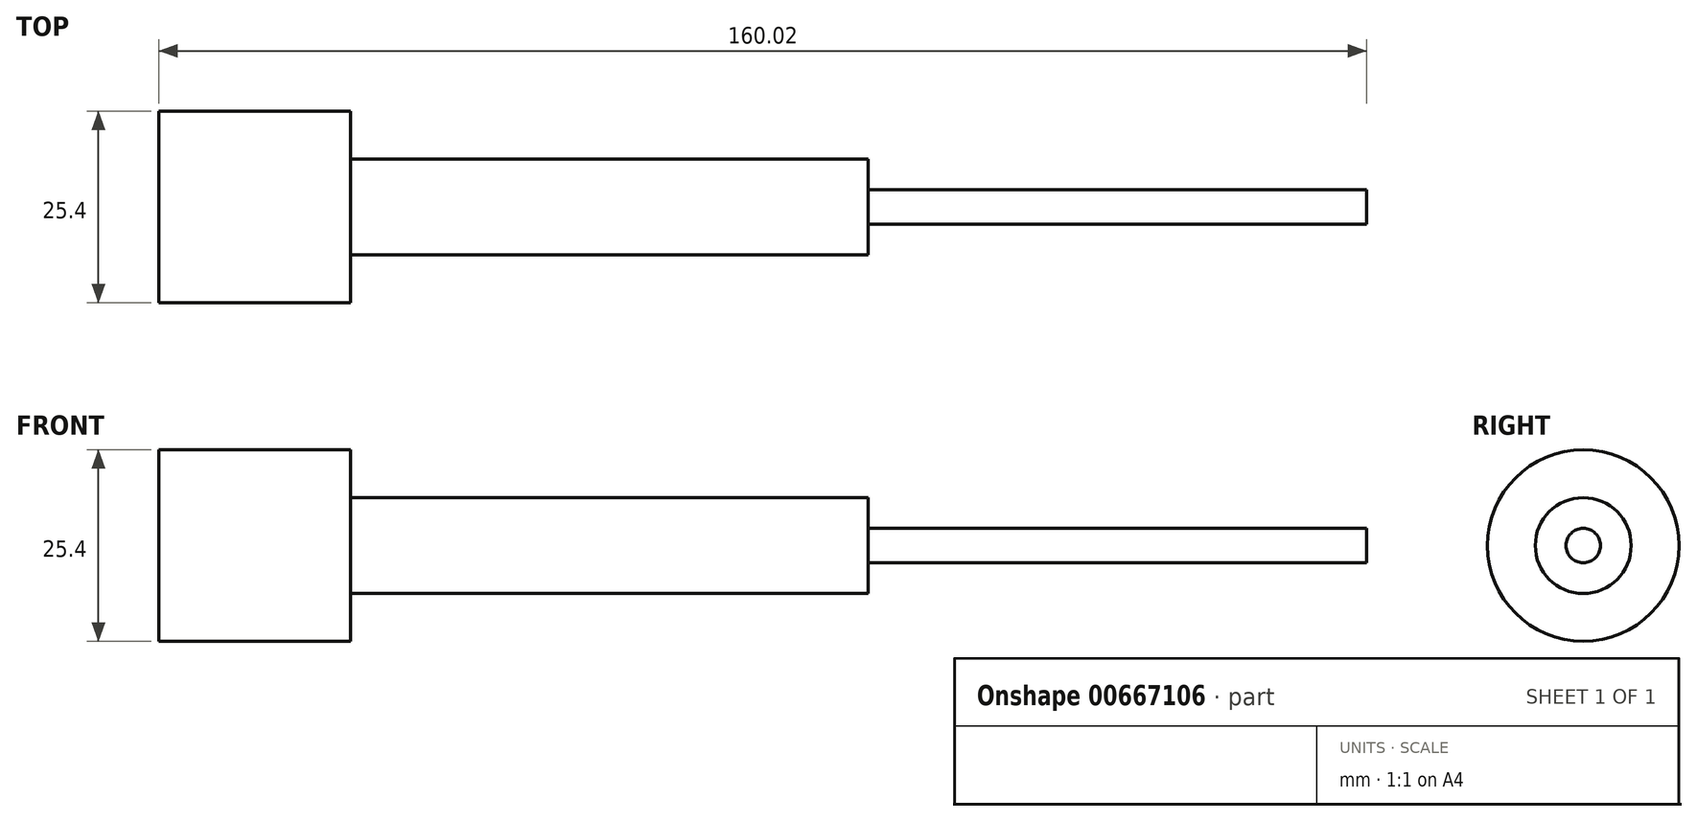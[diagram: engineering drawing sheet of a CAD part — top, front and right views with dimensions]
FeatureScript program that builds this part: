
annotation { "Feature Type Name" : "Feature", "Feature Type Description" : "" }
export const myFeature = defineFeature(function(context is Context, id is Id, definition is map)
    precondition{}
    {
        {
            var Q0;
            Q0=qCreatedBy(makeId("Right.planeOp"),FACE);
            var sketch = newSketch(context, id + "F0", { "sketchPlane" : qUnion([Q0])});
            skCircle(sketch, "E0", {"center": v(0, 0) * mm, "radius": 12.7 * mm});
            skSolve(sketch);
        }
        {
            var Q0;
            Q0 = qSketchRegion(id + "F0", true);
            extrude(context, id + "F1", {"entities" : qUnion([Q0]), "oppositeDirection" : true, "depth" : 160.02 * mm, "offsetDistance" : 25.4 * mm});
        }
        {
            var Q0;
            Q0=makeQuery(id+"F1.opExtrude","CAP_FACE",FACE,{"disambiguationData":[OSD([sQuery(id+"F0.wireOp",EDGE,"E0")])],"isStart":true});
            var sketch = newSketch(context, id + "F2", { "sketchPlane" : qUnion([Q0])});
            skCircle(sketch, "E1", {"center": v(0, 0) * mm, "radius": 6.35 * mm});
            skSolve(sketch);
        }
        {
            var Q0;
            Q0=makeQuery(id+"F2.imprint","IMPRINT",FACE,{"disambiguationData":[TD([[makeQuery(id+"F2.imprint","IMPRINT",EDGE,{"derivedFrom":sQuery(id+"F2.wireOp",EDGE,"E1")}),-1.0]])]});
            extrude(context, id + "F3", {"entities" : qUnion([Q0]), "operationType" : NewBodyOperationType.REMOVE, "oppositeDirection" : true, "depth" : 134.62 * mm, "offsetDistance" : 25.4 * mm});
        }
        {
            var Q0;
            Q0=makeQuery(id+"F1.opExtrude","CAP_FACE",FACE,{"disambiguationData":[OSD([sQuery(id+"F0.wireOp",EDGE,"E0")])],"isStart":true});
            var sketch = newSketch(context, id + "F4", { "sketchPlane" : qUnion([Q0])});
            skCircle(sketch, "E2", {"center": v(0, 0) * mm, "radius": 2.29 * mm});
            skSolve(sketch);
        }
        {
            var Q0;
            Q0=makeQuery(id+"F4.imprint","IMPRINT",FACE,{"disambiguationData":[TD([[makeQuery(id+"F4.imprint","IMPRINT",EDGE,{"derivedFrom":sQuery(id+"F4.wireOp",EDGE,"E2")}),-1.0]])]});
            extrude(context, id + "F5", {"entities" : qUnion([Q0]), "operationType" : NewBodyOperationType.REMOVE, "oppositeDirection" : true, "depth" : 66.04 * mm, "offsetDistance" : 25.4 * mm});
        }
    });
